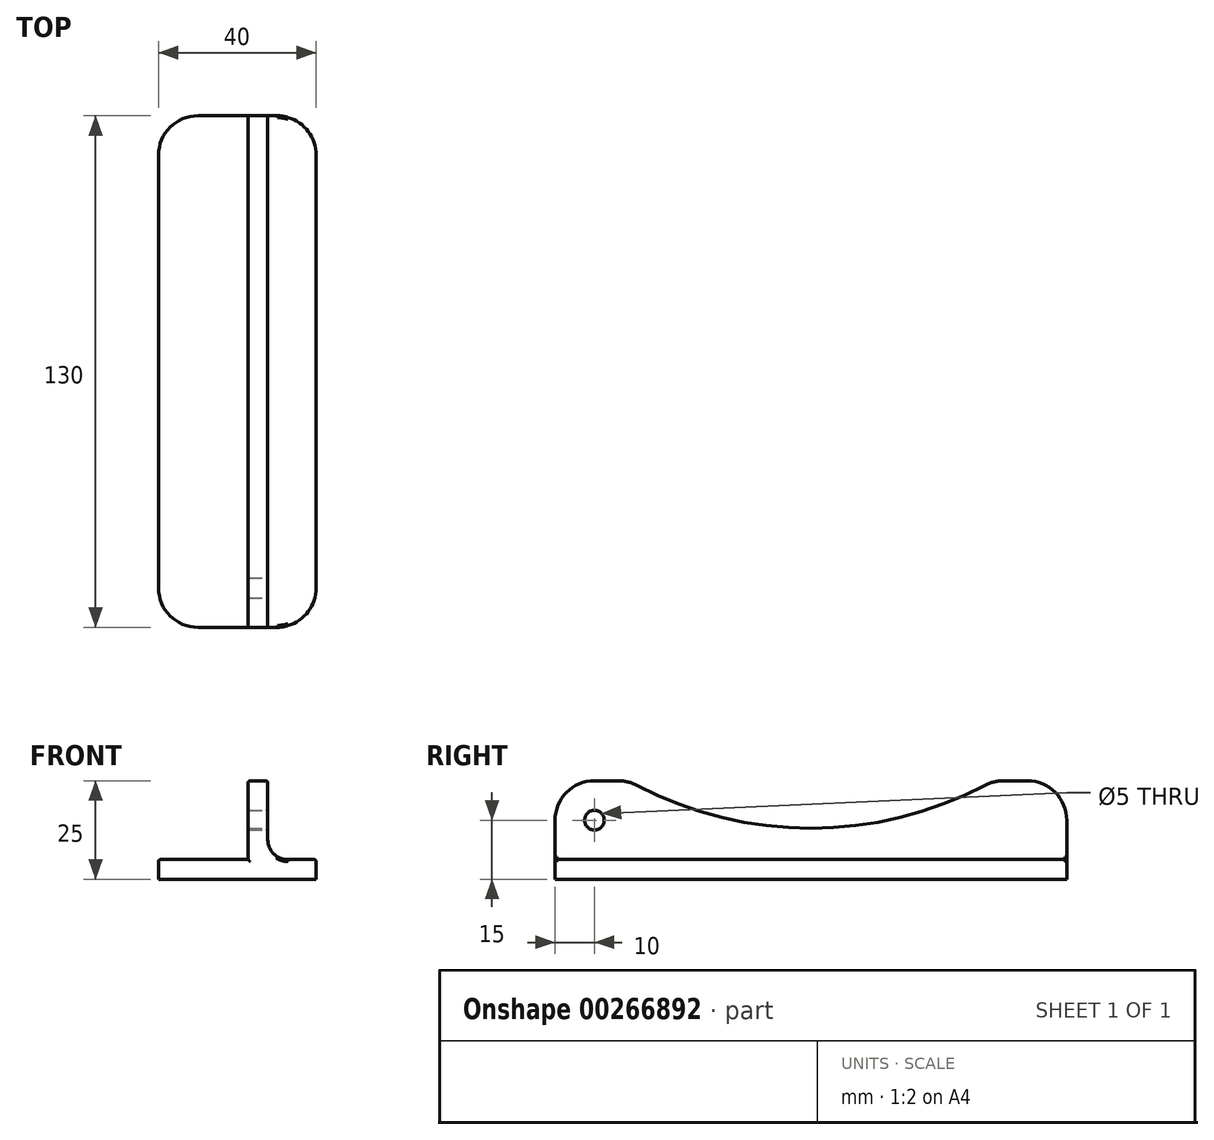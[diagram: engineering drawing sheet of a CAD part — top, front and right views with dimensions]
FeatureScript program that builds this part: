
annotation { "Feature Type Name" : "Feature", "Feature Type Description" : "" }
export const myFeature = defineFeature(function(context is Context, id is Id, definition is map)
    precondition{}
    {
        {
            var Q0;
            Q0=qCreatedBy(makeId("Top.planeOp"),FACE);
            var sketch = newSketch(context, id + "F0", { "sketchPlane" : qUnion([Q0])});
            skLineSegment(sketch, "E0.bottom", {"start": v(20, 65) * mm, "end": v(-20, 65) * mm});
            skLineSegment(sketch, "E0.top", {"start": v(20, -65) * mm, "end": v(-20, -65) * mm});
            skLineSegment(sketch, "E0.left", {"start": v(20, 65) * mm, "end": v(20, -65) * mm});
            skLineSegment(sketch, "E0.right", {"start": v(-20, 65) * mm, "end": v(-20, -65) * mm});
            skPoint(sketch, "E0.middle", {"position": v(0, 0) * mm});
            skSolve(sketch);
        }
        {
            var Q0;
            Q0 = qSketchRegion(id + "F0", true);
            extrude(context, id + "F1", {"entities" : qUnion([Q0]), "depth" : 2.5 * mm, "hasSecondDirection" : true, "secondDirectionOppositeDirection" : true, "secondDirectionDepth" : 2.5 * mm});
        }
        {
            var Q0;
            Q0=makeQuery(id+"F1.opExtrude","CAP_FACE",FACE,{"disambiguationData":[OSD([sQuery(id+"F0.wireOp",EDGE,"E0.bottom"),sQuery(id+"F0.wireOp",EDGE,"E0.top"),sQuery(id+"F0.wireOp",EDGE,"E0.left"),sQuery(id+"F0.wireOp",EDGE,"E0.right")])],"isStart":false});
            var sketch = newSketch(context, id + "F2", { "sketchPlane" : qUnion([Q0])});
            skLineSegment(sketch, "E1.bottom", {"start": v(2.75, 65) * mm, "end": v(7.75, 65) * mm});
            skLineSegment(sketch, "E1.top", {"start": v(2.75, -65) * mm, "end": v(7.75, -65) * mm});
            skLineSegment(sketch, "E1.left", {"start": v(2.75, 65) * mm, "end": v(2.75, -65) * mm});
            skLineSegment(sketch, "E1.right", {"start": v(7.75, 65) * mm, "end": v(7.75, -65) * mm});
            skSolve(sketch);
        }
        {
            var Q0;
            Q0 = qSketchRegion(id + "F2", true);
            extrude(context, id + "F3", {"entities" : qUnion([Q0]), "operationType" : NewBodyOperationType.ADD, "depth" : 20 * mm});
        }
        {
            var Q0;
            Q0=makeQuery(id+"F3.opExtrude","SWEPT_FACE",FACE,{"disambiguationData":[OSD([sQuery(id+"F2.wireOp",EDGE,"E1.right")])]});
            var sketch = newSketch(context, id + "F4", { "sketchPlane" : qUnion([Q0])});
            skCircle(sketch, "E2", {"center": v(-55, 12.5) * mm, "radius": 2.5 * mm});
            skCircle(sketch, "E3", {"center": v(-55, 12.5) * mm, "radius": 8 * mm, "construction": true});
            skSolve(sketch);
        }
        {
            var Q0;
            Q0 = qSketchRegion(id + "F4", true);
            extrude(context, id + "F5", {"entities" : qUnion([Q0]), "operationType" : NewBodyOperationType.REMOVE, "endBound" : BoundingType.THROUGH_ALL, "oppositeDirection" : true, "depth" : 25 * mm});
        }
        {
            var Q0;
            Q0=makeQuery(id+"F3.opExtrude","SWEPT_FACE",FACE,{"disambiguationData":[OSD([sQuery(id+"F2.wireOp",EDGE,"E1.right")])]});
            var sketch = newSketch(context, id + "F6", { "sketchPlane" : qUnion([Q0])});
            skCircle(sketch, "E4", {"center": v(-55, 12.5) * mm, "radius": 8 * mm, "construction": true});
            skCircle(sketch, "E5", {"center": v(55, 12.5) * mm, "radius": 8 * mm, "construction": true});
            skCircle(sketch, "E6", {"center": v(0, 105.45) * mm, "radius": 100 * mm, "construction": true});
            skCircle(sketch, "E7", {"center": v(0, 105.45) * mm, "radius": 95 * mm});
            skSolve(sketch);
        }
        {
            var Q0;
            Q0 = qSketchRegion(id + "F6", true);
            var Q1;
            Q1=makeQuery(id+"F3.opExtrude","SWEPT_FACE",FACE,{"disambiguationData":[OSD([sQuery(id+"F2.wireOp",EDGE,"E1.left")])]});
            extrude(context, id + "F7", {"entities" : qUnion([Q0]), "operationType" : NewBodyOperationType.REMOVE, "endBound" : BoundingType.UP_TO_SURFACE, "oppositeDirection" : true, "endBoundEntityFace" : qUnion([Q1]), "depth" : 25 * mm});
        }
        {
            var Q0;
            Q0=makeQuery(id+"F1.opExtrude","SWEPT_EDGE",EDGE,{"disambiguationData":[OSD([sQuery(id+"F0.wireOp",EDGE,"E0.bottom"),sQuery(id+"F0.wireOp",EDGE,"E0.right")])]});
            var Q1;
            Q1=makeQuery(id+"F1.opExtrude","SWEPT_EDGE",EDGE,{"disambiguationData":[OSD([sQuery(id+"F0.wireOp",EDGE,"E0.top"),sQuery(id+"F0.wireOp",EDGE,"E0.right")])]});
            var Q2;
            Q2=makeQuery(id+"F1.opExtrude","SWEPT_EDGE",EDGE,{"disambiguationData":[OSD([sQuery(id+"F0.wireOp",EDGE,"E0.bottom"),sQuery(id+"F0.wireOp",EDGE,"E0.left")])]});
            var Q3;
            Q3=makeQuery(id+"F1.opExtrude","SWEPT_EDGE",EDGE,{"disambiguationData":[OSD([sQuery(id+"F0.wireOp",EDGE,"E0.top"),sQuery(id+"F0.wireOp",EDGE,"E0.left")])]});
            var Q4;
            Q4=makeQuery(id+"F3.opExtrude","CAP_EDGE",EDGE,{"disambiguationData":[OSD([sQuery(id+"F2.wireOp",EDGE,"E1.bottom")])],"isStart":false});
            var Q5;
            Q5=makeQuery(id+"F3.opExtrude","CAP_EDGE",EDGE,{"disambiguationData":[OSD([sQuery(id+"F2.wireOp",EDGE,"E1.top")])],"isStart":false});
            var Q6;
            Q6=makeQuery(id+"F7.boolean.opBoolean","INTERSECT",EDGE,{"disambiguationData":[OD(1.0)],"derivedFrom":[makeQuery(id+"F3.opExtrude","CAP_FACE",FACE,{"disambiguationData":[OSD([sQuery(id+"F2.wireOp",EDGE,"E1.bottom"),sQuery(id+"F2.wireOp",EDGE,"E1.top"),sQuery(id+"F2.wireOp",EDGE,"E1.left"),sQuery(id+"F2.wireOp",EDGE,"E1.right")])],"isStart":false}),makeQuery(id+"F7.opExtrude","SWEPT_FACE",FACE,{"disambiguationData":[OSD([sQuery(id+"F6.wireOp",EDGE,"E7")])]})]});
            var Q7;
            Q7=makeQuery(id+"F7.boolean.opBoolean","INTERSECT",EDGE,{"disambiguationData":[OD(0.0)],"derivedFrom":[makeQuery(id+"F3.opExtrude","CAP_FACE",FACE,{"disambiguationData":[OSD([sQuery(id+"F2.wireOp",EDGE,"E1.bottom"),sQuery(id+"F2.wireOp",EDGE,"E1.top"),sQuery(id+"F2.wireOp",EDGE,"E1.left"),sQuery(id+"F2.wireOp",EDGE,"E1.right")])],"isStart":false}),makeQuery(id+"F7.opExtrude","SWEPT_FACE",FACE,{"disambiguationData":[OSD([sQuery(id+"F6.wireOp",EDGE,"E7")])]})]});
            var Q8;
            Q8=makeQuery(id+"FaIHQREa0zAQ9Ww_1.1.F3.opExtrude","CAP_EDGE",EDGE,{"disambiguationData":[OSD([sQuery(id+"F2.wireOp",EDGE,"E1.top")])],"isStart":false});
            var Q9;
            Q9=makeQuery(id+"FaIHQREa0zAQ9Ww_1.1.F3.opExtrude","CAP_EDGE",EDGE,{"disambiguationData":[OSD([sQuery(id+"F2.wireOp",EDGE,"E1.bottom")])],"isStart":false});
            fillet(context, id + "F8", {"entities" : qUnion([Q0, Q1, Q2, Q3, Q4, Q5, Q6, Q7, Q8, Q9]), "radius" : 10 * mm, "tangentPropagation" : true, "allowEdgeOverflow" : false});
        }
        {
            var Q0;
            Q0=makeQuery(id+"F3.opExtrude","CAP_EDGE",EDGE,{"disambiguationData":[OSD([sQuery(id+"F2.wireOp",EDGE,"E1.right")])],"isStart":true});
            var Q1;
            Q1=makeQuery(id+"FaIHQREa0zAQ9Ww_1.1.F3.opExtrude","CAP_EDGE",EDGE,{"disambiguationData":[OSD([sQuery(id+"F2.wireOp",EDGE,"E1.right")])],"isStart":true});
            fillet(context, id + "F9", {"entities" : qUnion([Q0, Q1]), "radius" : 5 * mm, "tangentPropagation" : true, "allowEdgeOverflow" : false});
        }
        {
            var Q0;
            Q0=makeQuery(id+"FaIHQREa0zAQ9Ww_1.1.F3.opExtrude","CAP_EDGE",EDGE,{"disambiguationData":[OSD([sQuery(id+"F2.wireOp",EDGE,"E1.right")])],"isStart":false});
            var Q1;
            Q1=makeQuery(id+"FaIHQREa0zAQ9Ww_1.1.F3.opExtrude","CAP_EDGE",EDGE,{"disambiguationData":[OSD([sQuery(id+"F2.wireOp",EDGE,"E1.left")])],"isStart":false});
            var Q2;
            Q2=makeQuery(id+"F8.opFillet","BLEND_EDGE",EDGE,{"blendedFrom":[makeQuery(id+"F3.opExtrude","CAP_EDGE",EDGE,{"disambiguationData":[OSD([sQuery(id+"F2.wireOp",EDGE,"E1.top")])],"isStart":false}),makeQuery(id+"F3.opExtrude","SWEPT_FACE",FACE,{"disambiguationData":[OSD([sQuery(id+"F2.wireOp",EDGE,"E1.left")])]})],"blendedInto":[makeQuery(id+"F3.opExtrude","SWEPT_FACE",FACE,{"disambiguationData":[OSD([sQuery(id+"F2.wireOp",EDGE,"E1.left")])]})]});
            var Q3;
            Q3=makeQuery(id+"F8.opFillet","BLEND_EDGE",EDGE,{"blendedFrom":[makeQuery(id+"F3.opExtrude","CAP_EDGE",EDGE,{"disambiguationData":[OSD([sQuery(id+"F2.wireOp",EDGE,"E1.top")])],"isStart":false}),makeQuery(id+"F3.opExtrude","SWEPT_FACE",FACE,{"disambiguationData":[OSD([sQuery(id+"F2.wireOp",EDGE,"E1.right")])]})],"blendedInto":[makeQuery(id+"F3.opExtrude","SWEPT_FACE",FACE,{"disambiguationData":[OSD([sQuery(id+"F2.wireOp",EDGE,"E1.right")])]})]});
            var Q4;
            {var subQ2=sQuery(id+"F0.wireOp",EDGE,"E0.top");var subQ4=sQuery(id+"F2.wireOp",EDGE,"E1.left");var subQ5=makeQuery(id+"F3.opExtrude","SWEPT_FACE",FACE,{"disambiguationData":[OSD([subQ4])]});var subQ6=sQuery(id+"F0.wireOp",EDGE,"E0.right");Q4=makeQuery(id+"FaIHQREa0zAQ9Ww_1.1.F3.boolean.opBoolean","SPLIT",EDGE,{"disambiguationData":[TD([subQ5])],"derivedFrom":makeQuery(id+"F3.boolean.opBoolean","SPLIT",EDGE,{"disambiguationData":[TD([makeQuery(id+"F1.opExtrude","SWEPT_FACE",FACE,{"disambiguationData":[OSD([subQ6])]})])],"derivedFrom":makeQuery(id+"F1.opExtrude","CAP_EDGE",EDGE,{"disambiguationData":[OSD([subQ2])],"isStart":false})})});}
            var Q5;
            {var subQ2=sQuery(id+"F2.wireOp",EDGE,"E1.left");var subQ3=makeQuery(id+"F3.opExtrude","SWEPT_FACE",FACE,{"disambiguationData":[OSD([subQ2])]});var subQ4=sQuery(id+"F0.wireOp",EDGE,"E0.right");var subQ5=sQuery(id+"F0.wireOp",EDGE,"E0.bottom");Q5=makeQuery(id+"FaIHQREa0zAQ9Ww_1.1.F3.boolean.opBoolean","SPLIT",EDGE,{"disambiguationData":[TD([subQ3])],"derivedFrom":makeQuery(id+"F3.boolean.opBoolean","SPLIT",EDGE,{"disambiguationData":[TD([makeQuery(id+"F1.opExtrude","SWEPT_FACE",FACE,{"disambiguationData":[OSD([subQ4])]})])],"derivedFrom":makeQuery(id+"F1.opExtrude","CAP_EDGE",EDGE,{"disambiguationData":[OSD([subQ5])],"isStart":false})})});}
            var Q6;
            Q6=makeQuery(id+"FRNCRCebRvEqaBn_1.1.F5.boolean.opBoolean","COPY",FACE,{"disambiguationData":[TD([makeQuery(id+"FaIHQREa0zAQ9Ww_1.1.F3.opExtrude","SWEPT_FACE",FACE,{"disambiguationData":[OSD([sQuery(id+"F2.wireOp",EDGE,"E1.left")])]})])],"derivedFrom":makeQuery(id+"FRNCRCebRvEqaBn_1.1.F5.opExtrude","SWEPT_FACE",FACE,{"disambiguationData":[OSD([sQuery(id+"F4.wireOp",EDGE,"E2")])]})});
            var Q7;
            Q7=makeQuery(id+"FRNCRCebRvEqaBn_1.1.F5.boolean.opBoolean","COPY",FACE,{"disambiguationData":[TD([makeQuery(id+"F3.opExtrude","SWEPT_FACE",FACE,{"disambiguationData":[OSD([sQuery(id+"F2.wireOp",EDGE,"E1.left")])]})])],"derivedFrom":makeQuery(id+"FRNCRCebRvEqaBn_1.1.F5.opExtrude","SWEPT_FACE",FACE,{"disambiguationData":[OSD([sQuery(id+"F4.wireOp",EDGE,"E2")])]})});
            var Q8;
            Q8=makeQuery(id+"F5.boolean.opBoolean","COPY",FACE,{"disambiguationData":[TD([makeQuery(id+"FaIHQREa0zAQ9Ww_1.1.F3.opExtrude","SWEPT_FACE",FACE,{"disambiguationData":[OSD([sQuery(id+"F2.wireOp",EDGE,"E1.left")])]})])],"derivedFrom":makeQuery(id+"F5.opExtrude","SWEPT_FACE",FACE,{"disambiguationData":[OSD([sQuery(id+"F4.wireOp",EDGE,"E2")])]})});
            var Q9;
            Q9=makeQuery(id+"F5.boolean.opBoolean","COPY",FACE,{"disambiguationData":[TD([makeQuery(id+"F3.opExtrude","SWEPT_FACE",FACE,{"disambiguationData":[OSD([sQuery(id+"F2.wireOp",EDGE,"E1.left")])]})])],"derivedFrom":makeQuery(id+"F5.opExtrude","SWEPT_FACE",FACE,{"disambiguationData":[OSD([sQuery(id+"F4.wireOp",EDGE,"E2")])]})});
            fillet(context, id + "F10", {"entities" : qUnion([Q0, Q1, Q2, Q3, Q4, Q5, Q6, Q7, Q8, Q9]), "radius" : 0.5 * mm, "tangentPropagation" : true, "allowEdgeOverflow" : false});
        }
    });
